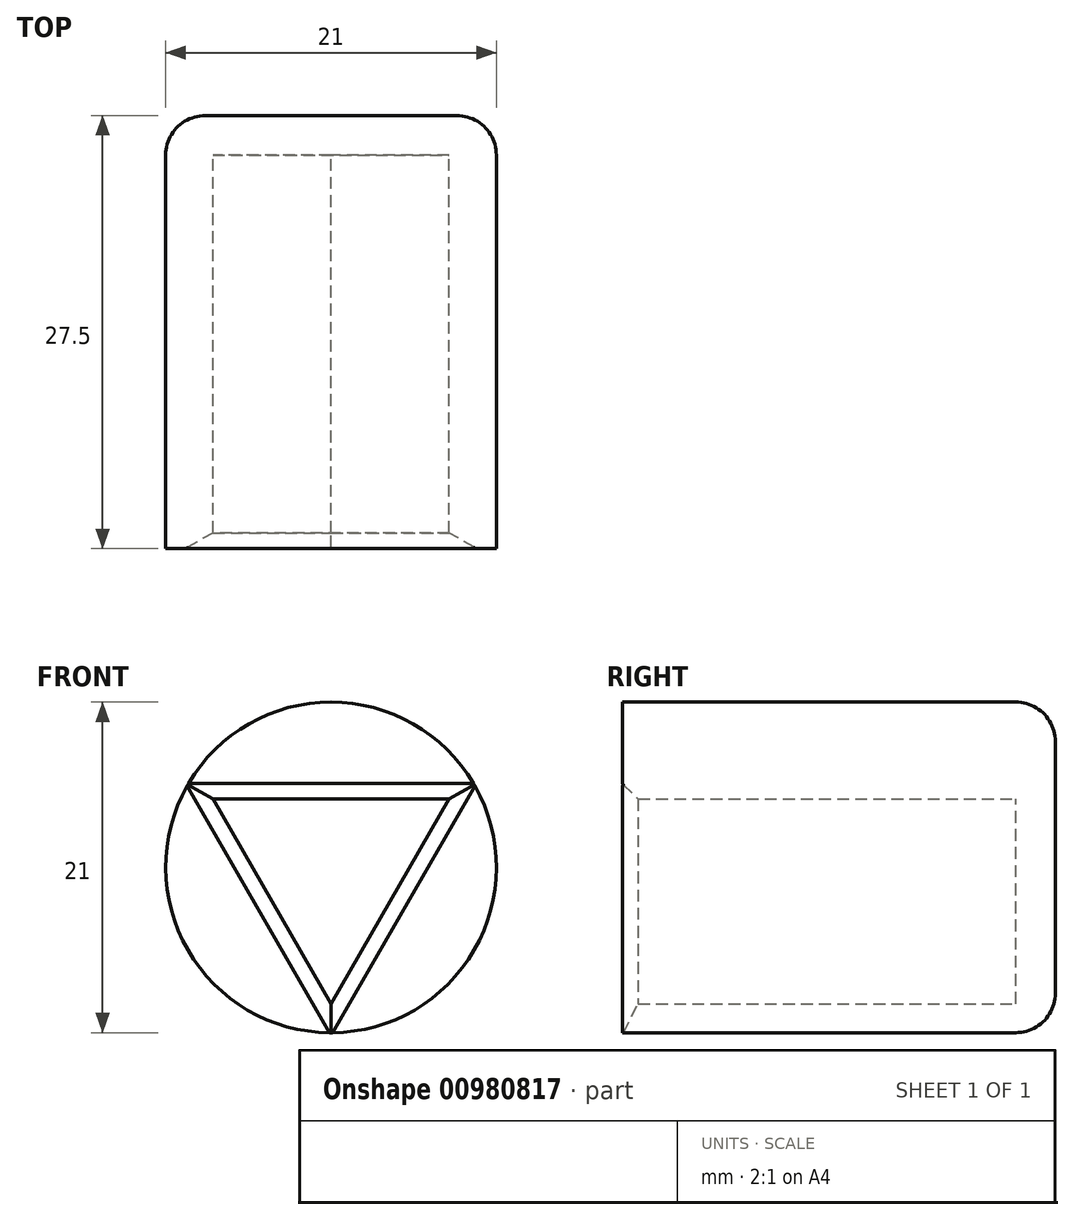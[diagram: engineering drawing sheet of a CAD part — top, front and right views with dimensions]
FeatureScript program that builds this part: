
annotation { "Feature Type Name" : "Feature", "Feature Type Description" : "" }
export const myFeature = defineFeature(function(context is Context, id is Id, definition is map)
    precondition{}
    {
        {
            var Q0;
            Q0=qCreatedBy(makeId("Front.planeOp"),FACE);
            var sketch = newSketch(context, id + "F0", { "sketchPlane" : qUnion([Q0])});
            skCircle(sketch, "E0.cCircle", {"center": v(0, 0) * mm, "radius": 4.33 * mm, "construction": true});
            skLineSegment(sketch, "E0.0", {"start": v(-7.5, 4.33) * mm, "end": v(7.5, 4.33) * mm});
            skLineSegment(sketch, "E0.1", {"start": v(7.5, 4.33) * mm, "end": v(0, -8.67) * mm});
            skLineSegment(sketch, "E0.2", {"start": v(0, -8.67) * mm, "end": v(-7.5, 4.33) * mm});
            skPoint(sketch, "E0.0.midPoint", {"position": v(0, 4.33) * mm});
            skCircle(sketch, "E1", {"center": v(0, 0) * mm, "radius": 10.5 * mm});
            skSolve(sketch);
        }
        {
            var Q0;
            Q0 = qSketchRegion(id + "F0", true);
            extrude(context, id + "F1", {"entities" : qUnion([Q0]), "depth" : 25 * mm, "offsetDistance" : 25 * mm});
        }
        {
            var Q0;
            Q0=qCreatedBy(makeId("Front.planeOp"),FACE);
            var sketch = newSketch(context, id + "F2", { "sketchPlane" : qUnion([Q0])});
            skCircle(sketch, "E2.0", {"center": v(0, 0) * mm, "radius": 10.5 * mm});
            skSolve(sketch);
        }
        {
            var Q0;
            Q0 = qSketchRegion(id + "F2", true);
            extrude(context, id + "F3", {"entities" : qUnion([Q0]), "operationType" : NewBodyOperationType.ADD, "oppositeDirection" : true, "depth" : 2.5 * mm, "offsetDistance" : 25 * mm});
        }
        {
            var Q0;
            Q0=makeQuery(id+"F3.opExtrude","CAP_EDGE",EDGE,{"disambiguationData":[OSD([sQuery(id+"F2.wireOp",EDGE,"E2.0")])],"isStart":false});
            fillet(context, id + "F4", {"entities" : qUnion([Q0]), "tangentPropagation" : true, "radius" : 2.5 * mm, "defaultsChanged" : true, "vertexSettings" : [], "allowEdgeOverflow" : false});
        }
        {
            var Q0;
            Q0=makeQuery(id+"F1.opExtrude","CAP_EDGE",EDGE,{"disambiguationData":[OSD([sQuery(id+"F0.wireOp",EDGE,"E0.2")])],"isStart":false});
            var Q1;
            Q1=makeQuery(id+"F1.opExtrude","CAP_EDGE",EDGE,{"disambiguationData":[OSD([sQuery(id+"F0.wireOp",EDGE,"E0.0")])],"isStart":false});
            var Q2;
            Q2=makeQuery(id+"F1.opExtrude","CAP_EDGE",EDGE,{"disambiguationData":[OSD([sQuery(id+"F0.wireOp",EDGE,"E0.1")])],"isStart":false});
            chamfer(context, id + "F5", {"entities" : qUnion([Q0, Q1, Q2]), "width" : 1 * mm, "tangentPropagation" : true});
        }
    });
